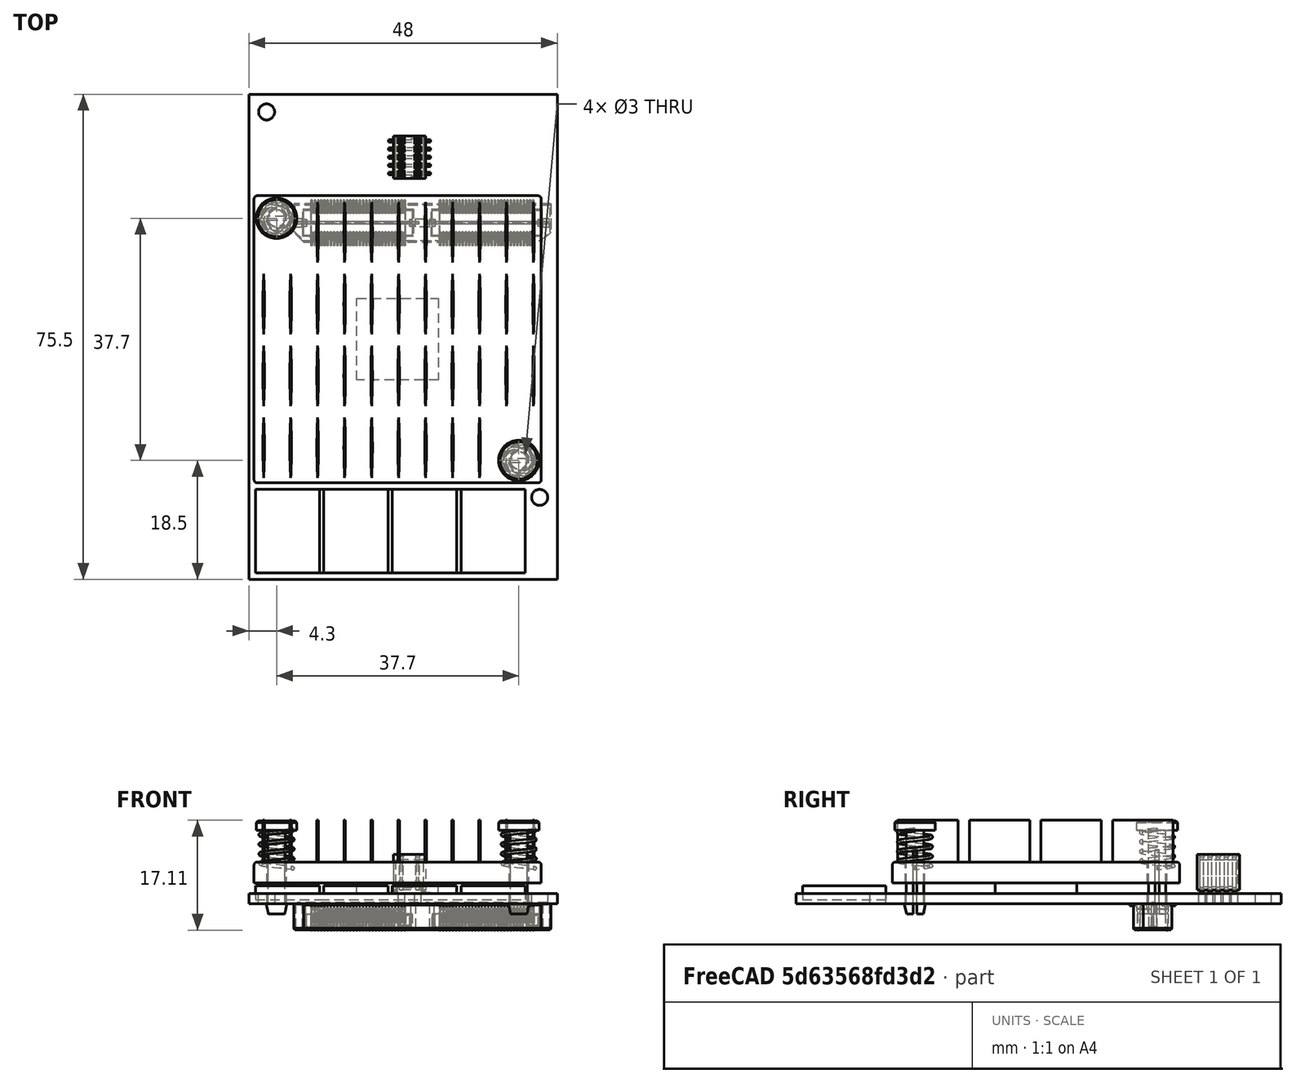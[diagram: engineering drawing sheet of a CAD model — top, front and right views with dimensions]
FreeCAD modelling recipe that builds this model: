
FCSTD DOCUMENT  (FreeCAD 0.17R13541 (Git))
Label: pimouss
License: All rights reserved
LicenseURL: http://en.wikipedia.org/wiki/All_rights_reserved
objects: Sketcher::SketchObject×15, PartDesign::Pad×7, PartDesign::Pocket×7, Part::Feature×7, PartDesign::LinearPattern×5, PartDesign::Body×5, PartDesign::MultiTransform×2, PartDesign::Revolution×2, PartDesign::Chamfer×2, Part::Sweep×2, PartDesign::Fillet×1, Part::Part2DObjectPython×1, App::Part×1
note: 72 computed .brp shape members not serialized (recipe doc carries the construction recipe); baked Part::Feature solids carry a one-line shape summary decoded from their .brp

FEATURE [Sketcher::SketchObject] Sketch008
  MapMode = 5
  Support = -> [XY_Plane001]
  sketch-geometry (4):
    g0: LineSegment StartX=-27 StartY=20 StartZ=0 EndX=21 EndY=20 EndZ=0
    g1: LineSegment StartX=21 StartY=20 StartZ=0 EndX=21 EndY=-55.5 EndZ=0
    g2: LineSegment StartX=21 StartY=-55.5 StartZ=0 EndX=-27 EndY=-55.5 EndZ=0
    g3: LineSegment StartX=-27 StartY=-55.5 StartZ=0 EndX=-27 EndY=20 EndZ=0
  constraints (12):
    c: Coincident(g0,g1)
    c: Coincident(g1,g2)
    c: Coincident(g2,g3)
    c: Coincident(g3,g0)
    c: Horizontal(g0)
    c: Horizontal(g2)
    c: Vertical(g1)
    c: Vertical(g3)
    c: Distance(g0) = 48
    c: Distance(g1) = 75.5
    c: Distance(g-1,g0) = 20
    c: Distance(g-1,g3) = 27
FEATURE [PartDesign::Pad] Pad003  label="pcb"
  Length = 1.6
  Length2 = 100
  Profile = -> Sketch008
  Type = 0
FEATURE [Sketcher::SketchObject] Sketch009
  MapMode = 5
  Placement = pos=(0,0,1.6) rot=(0,0,1;0rad)
  Support = -> [Pad003]
  expr: Constraints[11] = 40.5 - 16
  expr: Constraints[9] = 44.700000000000003 - 32
  expr: Constraints[10] = 18.5 - 16
  expr: Constraints[8] = 44.700000000000003 - 32
  sketch-geometry (4):
    g0: LineSegment StartX=-10.2 StartY=-11.8 StartZ=0 EndX=2.5 EndY=-11.8 EndZ=0
    g1: LineSegment StartX=2.5 StartY=-11.8 StartZ=0 EndX=2.5 EndY=-24.5 EndZ=0
    g2: LineSegment StartX=2.5 StartY=-24.5 StartZ=0 EndX=-10.2 EndY=-24.5 EndZ=0
    g3: LineSegment StartX=-10.2 StartY=-24.5 StartZ=0 EndX=-10.2 EndY=-11.8 EndZ=0
  constraints (12):
    c: Coincident(g0,g1)
    c: Coincident(g1,g2)
    c: Coincident(g2,g3)
    c: Coincident(g3,g0)
    c: Horizontal(g0)
    c: Horizontal(g2)
    c: Vertical(g1)
    c: Vertical(g3)
    c: Distance(g0) = 12.7
    c: Distance(g1) = 12.7
    c: Distance(g-1,g1) = 2.5
    c: Distance(g-1,g2) = 24.5
FEATURE [PartDesign::Pad] Pad005  label="chip"
  BaseFeature = -> Pad003
  Length = 1.6
  Length2 = 100
  Profile = -> Sketch009
  Type = 0
FEATURE [Sketcher::SketchObject] Sketch010
  MapMode = 5
  Placement = pos=(0,0,1.6) rot=(0,0,1;0rad)
  expr: Constraints[0] = 2.5 / 2
  sketch-geometry (4):
    g0: Circle CenterX=-24.25 CenterY=17.25 CenterZ=0 NormalX=0 NormalY=0 NormalZ=1 AngleXU=0 Radius=1.25
    g1: Circle CenterX=18.25 CenterY=-42.75 CenterZ=0 NormalX=0 NormalY=0 NormalZ=1 AngleXU=0 Radius=1.25
    g2: Circle CenterX=-22.7 CenterY=0.7 CenterZ=0 NormalX=0 NormalY=0 NormalZ=1 AngleXU=0 Radius=1.5
    g3: Circle CenterX=15 CenterY=-37 CenterZ=0 NormalX=0 NormalY=0 NormalZ=1 AngleXU=0 Radius=1.5
  constraints (12):
    c: Radius(g0) = 1.25
    c: Equal(g0,g1)
    c: DistanceY(g-1,g0) = 17.25
    c: DistanceY(g1,g-1) = 42.75
    c: DistanceX(g0,g-1) = 24.25
    c: DistanceX(g-1,g1) = 18.25
    c: Equal(g3,g2)
    c: Radius(g2) = 1.5
    c: DistanceX(g2,g-1) = 22.7
    c: DistanceY(g-1,g2) = 0.7
    c: DistanceX(g-1,g3) = 15
    c: DistanceY(g3,g-1) = 37
FEATURE [PartDesign::Pocket] Pocket005  label="main holes"
  BaseFeature = -> Pad005
  Length = 5
  Length2 = 100
  Profile = -> Sketch010
  Type = 1
FEATURE [Sketcher::SketchObject] Sketch011
  MapMode = 5
  Support = -> [XY_Plane002]
  expr: Constraints[11] = 44.700000000000003 - 40.5
  sketch-geometry (4):
    g0: LineSegment StartX=-26.2 StartY=4.2 StartZ=0 EndX=18.5 EndY=4.2 EndZ=0
    g1: LineSegment StartX=18.5 StartY=4.2 StartZ=0 EndX=18.5 EndY=-40.5 EndZ=0
    g2: LineSegment StartX=18.5 StartY=-40.5 StartZ=0 EndX=-26.2 EndY=-40.5 EndZ=0
    g3: LineSegment StartX=-26.2 StartY=-40.5 StartZ=0 EndX=-26.2 EndY=4.2 EndZ=0
  constraints (12):
    c: Coincident(g0,g1)
    c: Coincident(g1,g2)
    c: Coincident(g2,g3)
    c: Coincident(g3,g0)
    c: Horizontal(g0)
    c: Horizontal(g2)
    c: Vertical(g1)
    c: Vertical(g3)
    c: Distance(g0) = 44.7
    c: Equal(g0,g1)
    c: Distance(g-1,g1) = 18.5
    c: Distance(g-1,g0) = 4.2
FEATURE [PartDesign::Pad] Pad006  label="body"
  Length = 3.3
  Length2 = 100
  Profile = -> Sketch011
  Type = 0
  expr: Length = 4.9000000000000004 - 1.6000000000000001
FEATURE [PartDesign::Fillet] Fillet001  label="body fillet"
  Base = -> Pad006 [Edge4,Edge12,Edge7,Edge10,Edge1,Edge8,Edge2,Edge5]
  BaseFeature = -> Pad006
  Radius = 0.5
FEATURE [Sketcher::SketchObject] Sketch012
  ExternalGeometry = -> [Fillet001]
  MapMode = 5
  Placement = pos=(0,0,3.3) rot=(0,0,1;0rad)
  Support = -> [Fillet001]
  sketch-geometry (2):
    g0: ArcOfCircle CenterX=-113.185 CenterY=-1.5 CenterZ=0 NormalX=0 NormalY=0 NormalZ=1 AngleXU=0 Radius=88.61 StartAngle=6.23012 EndAngle=6.33625
    g1: ArcOfCircle CenterX=63.7853 CenterY=-1.5 CenterZ=0 NormalX=0 NormalY=0 NormalZ=1 AngleXU=0 Radius=88.61 StartAngle=3.08853 EndAngle=3.19466
  constraints (8):
    c: Coincident(g1,g0)
    c: Coincident(g1,g0)
    c: Equal(g0,g1)
    c: Vertical(g0,g0)
    c: DistanceY(g0,g0) = 9.4
    c: Radius(g1) = 88.61
    c: Distance(g0,g-3) = 1
    c: Distance(g0,g-4) = 0.5
FEATURE [PartDesign::Pad] Pad007  label="fin"
  BaseFeature = -> Fillet001
  Length = 6.5
  Length2 = 100
  Profile = -> Sketch012
  Type = 0
FEATURE [PartDesign::LinearPattern] LinearPattern  label="hfins"
  Direction = -> Sketch012 [H_Axis]
  Length = 42
  Occurrences = 11
FEATURE [PartDesign::LinearPattern] LinearPattern001  label="vfins"
  Direction = -> Sketch012 [V_Axis]
  Length = 33.5
  Occurrences = 4
  Reversed = true
FEATURE [PartDesign::MultiTransform] MultiTransform001  label="fins"
  BaseFeature = -> Pad007
  Originals = -> [Pad007]
  Transformations = -> [LinearPattern,LinearPattern001]
FEATURE [Sketcher::SketchObject] Sketch013
  ExternalGeometry = -> [MultiTransform001]
  MapMode = 5
  Placement = pos=(0,0,9.8) rot=(0,0,1;0rad)
  Support = -> [MultiTransform001]
  sketch-geometry (4):
    g0: LineSegment StartX=-24.8247 StartY=3.2 StartZ=0 EndX=-20.3753 EndY=3.2 EndZ=0
    g1: LineSegment StartX=-20.3753 StartY=3.2 StartZ=0 EndX=-20.3753 EndY=-6.68149 EndZ=0
    g2: LineSegment StartX=-20.3753 StartY=-6.68149 StartZ=0 EndX=-24.8247 EndY=-6.68149 EndZ=0
    g3: LineSegment StartX=-24.8247 StartY=-6.68149 StartZ=0 EndX=-24.8247 EndY=3.2 EndZ=0
  constraints (11):
    c: Coincident(g0,g1)
    c: Coincident(g1,g2)
    c: Coincident(g2,g3)
    c: Coincident(g3,g0)
    c: Horizontal(g0)
    c: Horizontal(g2)
    c: Vertical(g1)
    c: Vertical(g3)
    c: Tangent(g-3,g1)
    c: Tangent(g-4,g3)
    c: PointOnObject(g-3,g0)
FEATURE [PartDesign::Pocket] Pocket006  label="top left fin cut"
  BaseFeature = -> MultiTransform001
  Length = 0
  Length2 = 100
  Profile = -> Sketch013
  Type = 3
  UpToFace = -> MultiTransform001 [Face13]
FEATURE [Sketcher::SketchObject] Sketch014
  ExternalGeometry = -> [Pocket006]
  MapMode = 5
  Placement = pos=(0,0,9.8) rot=(0,0,1;0rad)
  Support = -> [Pocket006]
  sketch-geometry (4):
    g0: LineSegment StartX=12.9753 StartY=-30.3 StartZ=0 EndX=17.4247 EndY=-30.3 EndZ=0
    g1: LineSegment StartX=17.4247 StartY=-30.3 StartZ=0 EndX=17.4247 EndY=-39.7 EndZ=0
    g2: LineSegment StartX=17.4247 StartY=-39.7 StartZ=0 EndX=12.9753 EndY=-39.7 EndZ=0
    g3: LineSegment StartX=12.9753 StartY=-39.7 StartZ=0 EndX=12.9753 EndY=-30.3 EndZ=0
  constraints (12):
    c: Coincident(g0,g1)
    c: Coincident(g1,g2)
    c: Coincident(g2,g3)
    c: Coincident(g3,g0)
    c: Horizontal(g0)
    c: Horizontal(g2)
    c: Vertical(g1)
    c: Vertical(g3)
    c: Tangent(g-3,g1)
    c: Tangent(g-4,g3)
    c: PointOnObject(g-4,g0)
    c: PointOnObject(g-3,g2)
FEATURE [PartDesign::Pocket] Pocket007  label="bottom right fin cut"
  BaseFeature = -> Pocket006
  Length = 0
  Length2 = 100
  Profile = -> Sketch014
  Type = 3
  UpToFace = -> Pocket006 [Face13]
FEATURE [Sketcher::SketchObject] Sketch015
  ExternalGeometry = -> [Pocket007]
  MapMode = 5
  Placement = pos=(0,0,3.3) rot=(0,0,1;0rad)
  Support = -> [Pocket007]
  sketch-geometry (2):
    g0: Circle CenterX=-22.7 CenterY=0.7 CenterZ=0 NormalX=0 NormalY=0 NormalZ=1 AngleXU=0 Radius=1.5
    g1: Circle CenterX=15 CenterY=-37 CenterZ=0 NormalX=0 NormalY=0 NormalZ=1 AngleXU=0 Radius=1.5
  constraints (6):
    c: Equal(g0,g1)
    c: Radius(g1) = 1.5
    c: Distance(g0,g-6) = 3.5
    c: Distance(g0,g-3) = 3.5
    c: Distance(g1,g-4) = 3.5
    c: Distance(g1,g-5) = 3.5
FEATURE [PartDesign::Pocket] Pocket008  label="holes"
  BaseFeature = -> Pocket007
  Length = 0
  Length2 = 100
  Profile = -> Sketch015
  Type = 1
FEATURE [PartDesign::Body] Body002  label="radiator"
  Group = -> [Sketch011,Pad006,Fillet001,Sketch012,Pad007,MultiTransform001,LinearPattern,LinearPattern001,Sketch013,Pocket006,Sketch014,Pocket007,Sketch015,Pocket008]
  Origin = -> Origin002
  Placement = pos=(0,0,3.2) rot=(0,0,1;0rad)
  Tip = -> Pocket008
FEATURE [Sketcher::SketchObject] Sketch
  MapMode = 5
  Placement = pos=(0,0,0) rot=(1,0,0;1.5708rad)
  Support = -> [XZ_Plane002]
  expr: Constraints[19] = 2.6000000000000001 / 2
  expr: Constraints[9] = 6.2999999999999998 / 2
  expr: Constraints[18] = 3.2999999999999998 / 2
  expr: Constraints[10] = 2.7000000000000002 / 2
  sketch-geometry (8):
    g0: LineSegment StartX=-1.35 StartY=1.6 StartZ=0 EndX=-1.35 EndY=13 EndZ=0
    g1: LineSegment StartX=-1.35 StartY=13 StartZ=0 EndX=-3.15 EndY=13 EndZ=0
    g2: LineSegment StartX=-3.15 StartY=13 StartZ=0 EndX=-3.15 EndY=14.5 EndZ=0
    g3: LineSegment StartX=-3.15 StartY=14.5 StartZ=0 EndX=0 EndY=14.5 EndZ=0
    g4: LineSegment StartX=0 StartY=14.5 StartZ=0 EndX=0 EndY=0 EndZ=0
    g5: LineSegment StartX=-1.35 StartY=1.6 StartZ=0 EndX=-1.65 EndY=1.6 EndZ=0
    g6: LineSegment StartX=-1.65 StartY=1.6 StartZ=0 EndX=-1.3 EndY=0 EndZ=0
    g7: LineSegment StartX=-1.3 StartY=0 StartZ=0 EndX=0 EndY=0 EndZ=0
  constraints (23):
    c: Vertical(g0)
    c: Coincident(g0,g1)
    c: Horizontal(g1)
    c: Coincident(g1,g2)
    c: Vertical(g2)
    c: Coincident(g2,g3)
    c: Horizontal(g3)
    c: Coincident(g3,g4)
    c: Vertical(g4)
    c: Distance(g3) = 3.15
    c: Distance(g0,g4) = 1.35
    c: Distance(g2) = 1.5
    c: Distance(g4) = 14.5
    c: Horizontal(g5)
    c: Coincident(g5,g6)
    c: Coincident(g6,g7)
    c: Coincident(g7,g4)
    c: Horizontal(g7)
    c: Distance(g5,g4) = 1.65
    c: Distance(g7) = 1.3
    c: Coincident(g0,g5)
    c: Distance(g0,g7) = 1.6
    c: Coincident(g4,g-1)
FEATURE [PartDesign::Revolution] Revolution
  Angle = 360
  Axis = (0,0,1)
  Base = (0,0,0)
  Placement = pos=(0,0,0) rot=(1,0,0;1.5708rad)
  Profile = -> Sketch
  ReferenceAxis = -> Sketch [V_Axis]
FEATURE [PartDesign::Chamfer] Chamfer
  Base = -> Revolution [Edge5]
  BaseFeature = -> Revolution
  Placement = pos=(0,0,0) rot=(1,0,0;1.5708rad)
  Size = 0.25
FEATURE [Sketcher::SketchObject] Sketch016
  ExternalGeometry = -> [Chamfer]
  MapMode = 5
  Placement = pos=(0,0,0) rot=(1,0,0;3.14159rad)
  Support = -> [Chamfer]
  sketch-geometry (4):
    g0: LineSegment StartX=-1.65 StartY=0.3 StartZ=0 EndX=1.65 EndY=0.3 EndZ=0
    g1: LineSegment StartX=1.65 StartY=0.3 StartZ=0 EndX=1.65 EndY=-0.3 EndZ=0
    g2: LineSegment StartX=1.65 StartY=-0.3 StartZ=0 EndX=-1.65 EndY=-0.3 EndZ=0
    g3: LineSegment StartX=-1.65 StartY=-0.3 StartZ=0 EndX=-1.65 EndY=0.3 EndZ=0
  constraints (12):
    c: Coincident(g0,g1)
    c: Coincident(g1,g2)
    c: Coincident(g2,g3)
    c: Coincident(g3,g0)
    c: Horizontal(g0)
    c: Horizontal(g2)
    c: Vertical(g1)
    c: Vertical(g3)
    c: Tangent(g-3,g1)
    c: Tangent(g-3,g3)
    c: Distance(g1) = 0.6
    c: Distance(g-1,g0) = 0.3
FEATURE [PartDesign::Pocket] Pocket
  BaseFeature = -> Chamfer
  Length = 10
  Length2 = 100
  Placement = pos=(0,0,0) rot=(1,0,0;1.5708rad)
  Profile = -> Sketch016
  Type = 0
FEATURE [PartDesign::Body] Body  label="top left prong"
  Group = -> [Sketch,Revolution,Chamfer,Sketch016,Pocket]
  Origin = -> Origin003
  Placement = pos=(-22.7,0.7,-1.6) rot=(0,0,1;0rad)
  Tip = -> Pocket
FEATURE [Sketcher::SketchObject] Sketch017
  MapMode = 5
  Placement = pos=(0,0,0) rot=(1,0,0;1.5708rad)
  expr: Constraints[19] = 2.6000000000000001 / 2
  expr: Constraints[9] = 6.2999999999999998 / 2
  expr: Constraints[18] = 3.2999999999999998 / 2
  expr: Constraints[10] = 2.7000000000000002 / 2
  sketch-geometry (8):
    g0: LineSegment StartX=-1.35 StartY=1.6 StartZ=0 EndX=-1.35 EndY=13 EndZ=0
    g1: LineSegment StartX=-1.35 StartY=13 StartZ=0 EndX=-3.15 EndY=13 EndZ=0
    g2: LineSegment StartX=-3.15 StartY=13 StartZ=0 EndX=-3.15 EndY=14.5 EndZ=0
    g3: LineSegment StartX=-3.15 StartY=14.5 StartZ=0 EndX=0 EndY=14.5 EndZ=0
    g4: LineSegment StartX=0 StartY=14.5 StartZ=0 EndX=0 EndY=0 EndZ=0
    g5: LineSegment StartX=-1.35 StartY=1.6 StartZ=0 EndX=-1.65 EndY=1.6 EndZ=0
    g6: LineSegment StartX=-1.65 StartY=1.6 StartZ=0 EndX=-1.3 EndY=0 EndZ=0
    g7: LineSegment StartX=-1.3 StartY=0 StartZ=0 EndX=0 EndY=0 EndZ=0
  constraints (23):
    c: Vertical(g0)
    c: Coincident(g0,g1)
    c: Horizontal(g1)
    c: Coincident(g1,g2)
    c: Vertical(g2)
    c: Coincident(g2,g3)
    c: Horizontal(g3)
    c: Coincident(g3,g4)
    c: Vertical(g4)
    c: Distance(g3) = 3.15
    c: Distance(g0,g4) = 1.35
    c: Distance(g2) = 1.5
    c: Distance(g4) = 14.5
    c: Horizontal(g5)
    c: Coincident(g5,g6)
    c: Coincident(g6,g7)
    c: Coincident(g7,g4)
    c: Horizontal(g7)
    c: Distance(g5,g4) = 1.65
    c: Distance(g7) = 1.3
    c: Coincident(g0,g5)
    c: Distance(g0,g7) = 1.6
    c: Coincident(g4,g-1)
FEATURE [PartDesign::Revolution] Revolution001
  Angle = 360
  Axis = (0,0,1)
  Base = (0,0,0)
  Placement = pos=(0,0,0) rot=(1,0,0;1.5708rad)
  Profile = -> Sketch017
  ReferenceAxis = -> Sketch017 [V_Axis]
FEATURE [PartDesign::Chamfer] Chamfer001
  Base = -> Revolution001 [Edge5]
  BaseFeature = -> Revolution001
  Placement = pos=(0,0,0) rot=(1,0,0;1.5708rad)
  Size = 0.25
FEATURE [Sketcher::SketchObject] Sketch018
  ExternalGeometry = -> [Chamfer001]
  MapMode = 5
  Placement = pos=(0,0,0) rot=(1,0,0;3.14159rad)
  Support = -> [Chamfer001]
  sketch-geometry (4):
    g0: LineSegment StartX=-1.65 StartY=0.3 StartZ=0 EndX=1.65 EndY=0.3 EndZ=0
    g1: LineSegment StartX=1.65 StartY=0.3 StartZ=0 EndX=1.65 EndY=-0.3 EndZ=0
    g2: LineSegment StartX=1.65 StartY=-0.3 StartZ=0 EndX=-1.65 EndY=-0.3 EndZ=0
    g3: LineSegment StartX=-1.65 StartY=-0.3 StartZ=0 EndX=-1.65 EndY=0.3 EndZ=0
  constraints (12):
    c: Coincident(g0,g1)
    c: Coincident(g1,g2)
    c: Coincident(g2,g3)
    c: Coincident(g3,g0)
    c: Horizontal(g0)
    c: Horizontal(g2)
    c: Vertical(g1)
    c: Vertical(g3)
    c: Tangent(g-3,g1)
    c: Tangent(g-3,g3)
    c: Distance(g1) = 0.6
    c: Distance(g-1,g0) = 0.3
FEATURE [PartDesign::Pocket] Pocket009
  BaseFeature = -> Chamfer001
  Length = 10
  Length2 = 100
  Placement = pos=(0,0,0) rot=(1,0,0;1.5708rad)
  Profile = -> Sketch018
  Type = 0
FEATURE [PartDesign::Body] Body003  label="bottom right prong"
  Group = -> [Sketch017,Revolution001,Chamfer001,Sketch018,Pocket009]
  Origin = -> Origin004
  Placement = pos=(15,-37,-1.6) rot=(0,0,1;0rad)
  Tip = -> Pocket009
FEATURE [Part::Part2DObjectPython] BSpline  label="Spring (2.5 r)"  # Draft 2D object (typed FeaturePython)
  Closed = false
  MakeFace = true
  Parameterization = 1
  Points = (289) [(2.5,0,0),(2.49049,0.217889,0.0208333),(2.46202,0.43412,0.0416667),(2.41481,0.647048,0.0625),(2.34923,0.85505,0.0833333),(2.26577,1.05655,0.104167),+283 more]
FEATURE [Sketcher::SketchObject] Sketch019
  MapMode = 5
  Placement = pos=(0,0,0) rot=(1,0,0;1.5708rad)
  Support = -> [XZ_Plane002]
  sketch-geometry (1):
    g0: Circle CenterX=2.5 CenterY=0 CenterZ=0 NormalX=0 NormalY=0 NormalZ=1 AngleXU=0 Radius=0.25
  constraints (3):
    c: PointOnObject(g0,g-1)
    c: Radius(g0) = 0.25
    c: Distance(g0,g-1) = 2.5
FEATURE [Part::Sweep] Sweep  label="top left prong spring"
  Frenet = false
  Placement = pos=(-22.7,0.7,5.5) rot=(0,0,1;0rad)
  Sections = -> [Sketch019]
  Solid = true
  Spine = -> BSpline [Edge1]
  Transition = 1
FEATURE [Part::Sweep] Sweep001  label="bottom right prong spring"
  Frenet = false
  Placement = pos=(15,-37,5.5) rot=(0,0,1;0rad)
  Sections = -> [Sketch019]
  Solid = true
  Spine = -> BSpline [Edge1]
  Transition = 1
FEATURE [Part::Feature] Part__Feature  label="RSM-105-02-D_socket"
  Placement = pos=(-2,10.205,1.9) rot=(-0.57735,0.57735,0.57735;4.18879rad)
  shape: bbox 5.08 x 6.604 x 5.791 mm, 136 faces (baked)
FEATURE [Part::Feature] Part__Feature001  label="RSM-105-02-D_pins"
  Placement = pos=(-2,10.205,1.9) rot=(-0.57735,0.57735,0.57735;4.18879rad)
  shape: bbox 6.477 x 5.842 x 5.258 mm, 176 faces (baked)
FEATURE [Sketcher::SketchObject] Sketch020
  MapMode = 5
  Placement = pos=(0,0,1.6) rot=(0,0,1;0rad)
  Support = -> [Pocket005]
  expr: Constraints[4] = 1.27 * 2
  expr: Constraints[3] = 2.54 / 2
  sketch-geometry (2):
    g0: GeomPoint X=-2 Y=10.205 Z=0
    g1: Circle CenterX=-3.27 CenterY=12.745 CenterZ=0 NormalX=0 NormalY=0 NormalZ=1 AngleXU=0 Radius=0.5
  constraints (5):
    c: Distance(g0,g-1) = 10.205
    c: Distance(g0,g-2) = 2
    c: Radius(g1) = 0.5
    c: DistanceX(g1,g0) = 1.27
    c: DistanceY(g0,g1) = 2.54
FEATURE [PartDesign::Pocket] Pocket010
  BaseFeature = -> Pocket005
  Length = 5
  Length2 = 100
  Profile = -> Sketch020
  Type = 1
FEATURE [PartDesign::LinearPattern] LinearPattern002
  Direction = -> Sketch020 [H_Axis]
  Length = 2.54
  Occurrences = 2
FEATURE [PartDesign::LinearPattern] LinearPattern003
  Direction = -> Sketch020 [V_Axis]
  Length = 5.08
  Occurrences = 5
  Reversed = true
  expr: Length = 1.27 * 4
FEATURE [PartDesign::MultiTransform] MultiTransform
  BaseFeature = -> Pocket010
  Originals = -> [Pocket010]
  Transformations = -> [LinearPattern002,LinearPattern003]
FEATURE [PartDesign::Body] Body001  label="PCB"
  Group = -> [Sketch008,Pad003,Sketch009,Pad005,Sketch010,Pocket005,Sketch020,Pocket010,MultiTransform,LinearPattern002,LinearPattern003]
  Origin = -> Origin001
  Tip = -> MultiTransform
FEATURE [Sketcher::SketchObject] Sketch021
  MapMode = 5
  Support = -> [XY_Plane002]
  expr: Constraints[11] = 13 / 2
  sketch-geometry (4):
    g0: LineSegment StartX=-5 StartY=6.5 StartZ=0 EndX=5 EndY=6.5 EndZ=0
    g1: LineSegment StartX=5 StartY=6.5 StartZ=0 EndX=5 EndY=-6.5 EndZ=0
    g2: LineSegment StartX=5 StartY=-6.5 StartZ=0 EndX=-5 EndY=-6.5 EndZ=0
    g3: LineSegment StartX=-5 StartY=-6.5 StartZ=0 EndX=-5 EndY=6.5 EndZ=0
  constraints (12):
    c: Coincident(g0,g1)
    c: Coincident(g1,g2)
    c: Coincident(g2,g3)
    c: Coincident(g3,g0)
    c: Horizontal(g0)
    c: Horizontal(g2)
    c: Vertical(g1)
    c: Vertical(g3)
    c: Distance(g0) = 10
    c: Distance(g3) = 13
    c: Distance(g-1,g3) = 5
    c: Distance(g-1,g0) = 6.5
FEATURE [PartDesign::Pad] Pad
  Length = 1.2
  Length2 = 100
  Profile = -> Sketch021
  Type = 0
FEATURE [PartDesign::Pad] Pad008
  BaseFeature = -> Pad
  Length = 1
  Length2 = 100
  Profile = -> Pad [Face5]
  Type = 0
FEATURE [PartDesign::Pad] Pad009
  BaseFeature = -> Pad008
  Length = 32
  Length2 = 100
  Profile = -> Pad008 [Face8]
  Type = 0
FEATURE [PartDesign::LinearPattern] LinearPattern004
  BaseFeature = -> Pad009
  Direction = -> Sketch021 [H_Axis]
  Length = 32
  Occurrences = 4
  Originals = -> [Pad]
FEATURE [PartDesign::Body] Body004  label="ram"
  Group = -> [Sketch021,Pad,Pad008,Pad009,LinearPattern004]
  Origin = -> Origin006
  Placement = pos=(-21,-48,1.6) rot=(0,0,1;0rad)
  Tip = -> LinearPattern004
FEATURE [Part::Feature] Part__Feature002  label="QTH-060-01-F-D_socket"
  Placement = pos=(0,0,0) rot=(1,0,0;4.71239rad)
  shape: bbox 40.01 x 5.969 x 4.064 mm, 686 faces (baked)
FEATURE [Part::Feature] Part__Feature003  label="QTH-060-01-F-D_pins_r"
  Placement = pos=(2.65,2.12,-0.0762) rot=(-0.57735,-0.57735,0.57735;2.0944rad)
  shape: bbox 14.71 x 7.112 x 4.164 mm, 1198 faces (baked)
FEATURE [Part::Feature] Part__Feature004  label="QTH-060-01-F-D_pins_l"
  Placement = pos=(-17.35,2.12,-0.0762) rot=(-0.57735,-0.57735,0.57735;2.0944rad)
  shape: bbox 14.71 x 7.112 x 4.164 mm, 1198 faces (baked)
FEATURE [Part::Feature] Part__Feature005  label="QTH-060-01-F-D_gnd_r"
  Placement = pos=(10.0013,0,0) rot=(1,0,0;4.71239rad)
  shape: bbox 18.92 x 0.381 x 3.759 mm, 18 faces (baked)
FEATURE [Part::Feature] Part__Feature006  label="QTH-060-01-F-D_gnd_l"
  Placement = pos=(-10.0013,0,0) rot=(1,0,0;4.71239rad)
  shape: bbox 18.92 x 0.381 x 3.759 mm, 18 faces (baked)
FEATURE [App::Part] Part  label="pimouss"
  Group = -> [Body001,Body002,Body,Body003,BSpline,Sketch019,Sweep,Sweep001,Body004,Part__Feature,Part__Feature001,Part__Feature002,Part__Feature003,Part__Feature004,Part__Feature005,Part__Feature006]
  License = CC BY 3.0
  LicenseURL = http://creativecommons.org/licenses/by/3.0/
  Origin = -> Origin
